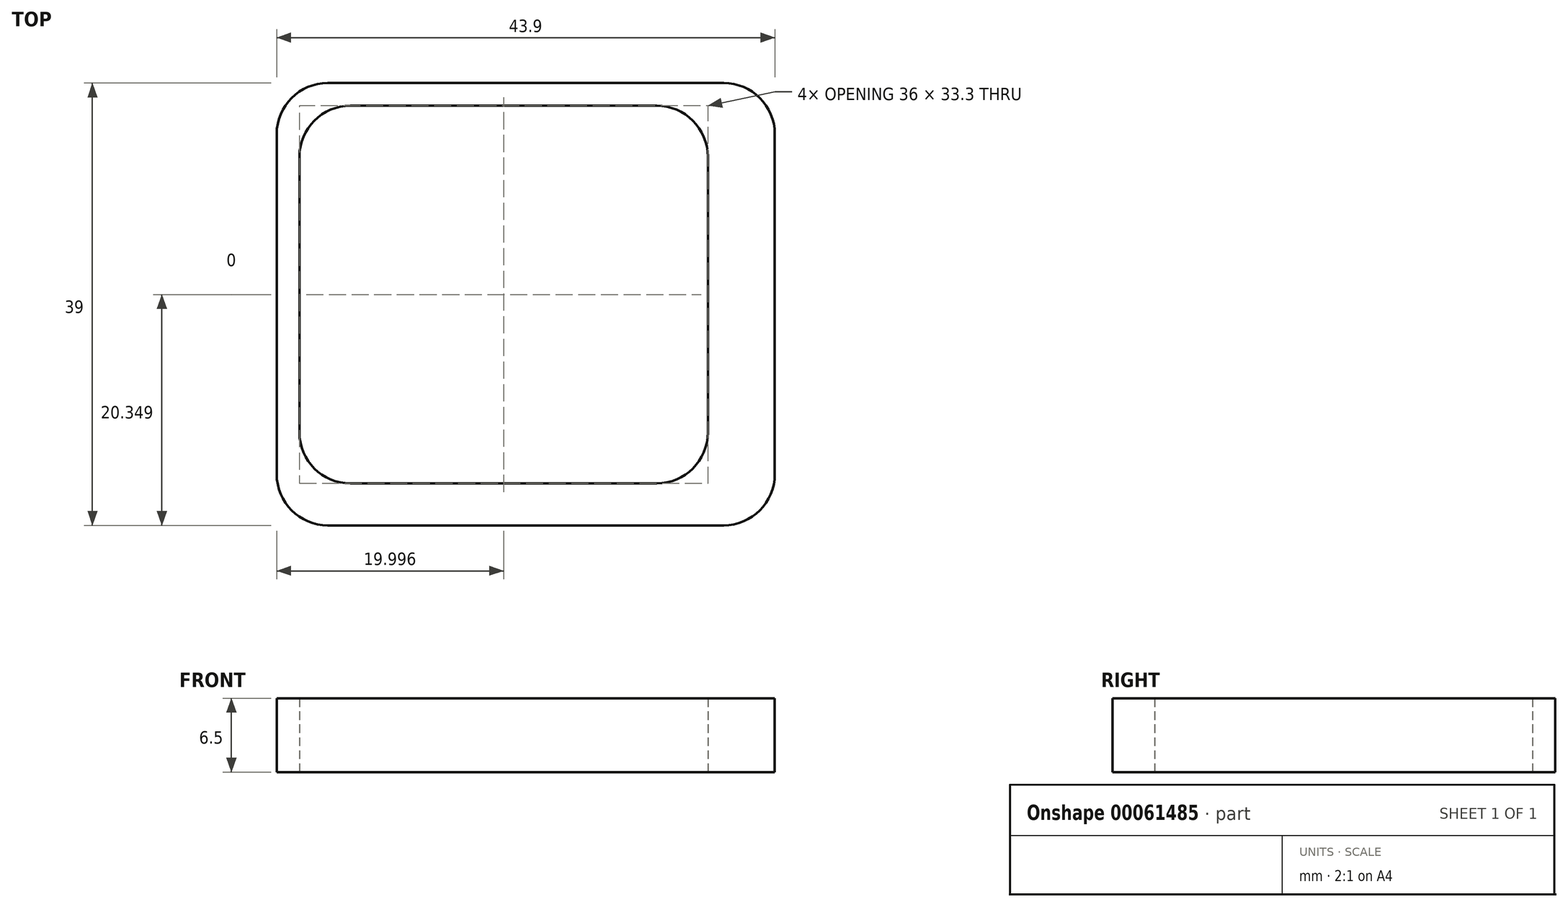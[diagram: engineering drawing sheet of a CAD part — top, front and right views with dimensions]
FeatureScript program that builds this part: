
annotation { "Feature Type Name" : "Feature", "Feature Type Description" : "" }
export const myFeature = defineFeature(function(context is Context, id is Id, definition is map)
    precondition{}
    {
        {
            var Q0;
            Q0=qCreatedBy(makeId("Top.planeOp"),FACE);
            var sketch = newSketch(context, id + "F0", { "sketchPlane" : qUnion([Q0])});
            skLineSegment(sketch, "E0.rect.bottom", {"start": v(17.94, -15.73) * mm, "end": v(-18.06, -15.73) * mm});
            skLineSegment(sketch, "E0.rect.top", {"start": v(17.94, 17.57) * mm, "end": v(-18.06, 17.57) * mm});
            skLineSegment(sketch, "E0.rect.left", {"start": v(17.94, -15.73) * mm, "end": v(17.94, 17.57) * mm});
            skLineSegment(sketch, "E0.rect.right", {"start": v(-18.06, -15.73) * mm, "end": v(-18.06, 17.57) * mm});
            skPoint(sketch, "E0.rect.middle", {"position": v(-0.06, 0.92) * mm});
            skLineSegment(sketch, "E1.0", {"start": v(23.84, 19.57) * mm, "end": v(-20.06, 19.57) * mm});
            skLineSegment(sketch, "E1.3", {"start": v(-20.06, -19.43) * mm, "end": v(-20.06, 19.57) * mm});
            skLineSegment(sketch, "E2", {"start": v(23.84, 19.57) * mm, "end": v(23.84, -19.43) * mm});
            skLineSegment(sketch, "E3", {"start": v(-20.06, -19.43) * mm, "end": v(23.84, -19.43) * mm});
            skSolve(sketch);
        }
        {
            var Q0;
            Q0=makeQuery(id+"F0.imprint","IMPRINT",FACE,{"disambiguationData":[TD([[makeQuery(id+"F0.imprint","IMPRINT",EDGE,{"derivedFrom":sQuery(id+"F0.wireOp",EDGE,"E0.rect.bottom")}),1.0]])]});
            extrude(context, id + "F1", {"entities" : qUnion([Q0]), "depth" : 6.5 * mm});
        }
        {
            var Q0;
            Q0=makeQuery(id+"F1.opExtrude","SWEPT_EDGE",EDGE,{"disambiguationData":[OSD([sQuery(id+"F0.wireOp",EDGE,"E0.rect.top"),sQuery(id+"F0.wireOp",EDGE,"E0.rect.right")])]});
            var Q1;
            Q1=makeQuery(id+"F1.opExtrude","SWEPT_EDGE",EDGE,{"disambiguationData":[OSD([sQuery(id+"F0.wireOp",EDGE,"E0.rect.bottom"),sQuery(id+"F0.wireOp",EDGE,"E0.rect.right")])]});
            var Q2;
            Q2=makeQuery(id+"F1.opExtrude","SWEPT_EDGE",EDGE,{"disambiguationData":[OSD([sQuery(id+"F0.wireOp",EDGE,"E0.rect.bottom"),sQuery(id+"F0.wireOp",EDGE,"E0.rect.left")])]});
            var Q3;
            Q3=makeQuery(id+"F1.opExtrude","SWEPT_EDGE",EDGE,{"disambiguationData":[OSD([sQuery(id+"F0.wireOp",EDGE,"E0.rect.top"),sQuery(id+"F0.wireOp",EDGE,"E0.rect.left")])]});
            var Q4;
            Q4=makeQuery(id+"F1.opExtrude","SWEPT_EDGE",EDGE,{"disambiguationData":[OSD([sQuery(id+"F0.wireOp",EDGE,"E2"),sQuery(id+"F0.wireOp",EDGE,"E3")])]});
            var Q5;
            Q5=makeQuery(id+"F1.opExtrude","SWEPT_EDGE",EDGE,{"disambiguationData":[OSD([sQuery(id+"F0.wireOp",EDGE,"E1.3"),sQuery(id+"F0.wireOp",EDGE,"E3")])]});
            var Q6;
            Q6=makeQuery(id+"F1.opExtrude","SWEPT_EDGE",EDGE,{"disambiguationData":[OSD([sQuery(id+"F0.wireOp",EDGE,"E1.0"),sQuery(id+"F0.wireOp",EDGE,"E2")])]});
            var Q7;
            Q7=makeQuery(id+"F1.opExtrude","SWEPT_EDGE",EDGE,{"disambiguationData":[OSD([sQuery(id+"F0.wireOp",EDGE,"E1.0"),sQuery(id+"F0.wireOp",EDGE,"E1.3")])]});
            fillet(context, id + "F2", {"entities" : qUnion([Q0, Q1, Q2, Q3, Q4, Q5, Q6, Q7]), "radius" : 4.5 * mm, "tangentPropagation" : true, "allowEdgeOverflow" : false});
        }
    });
